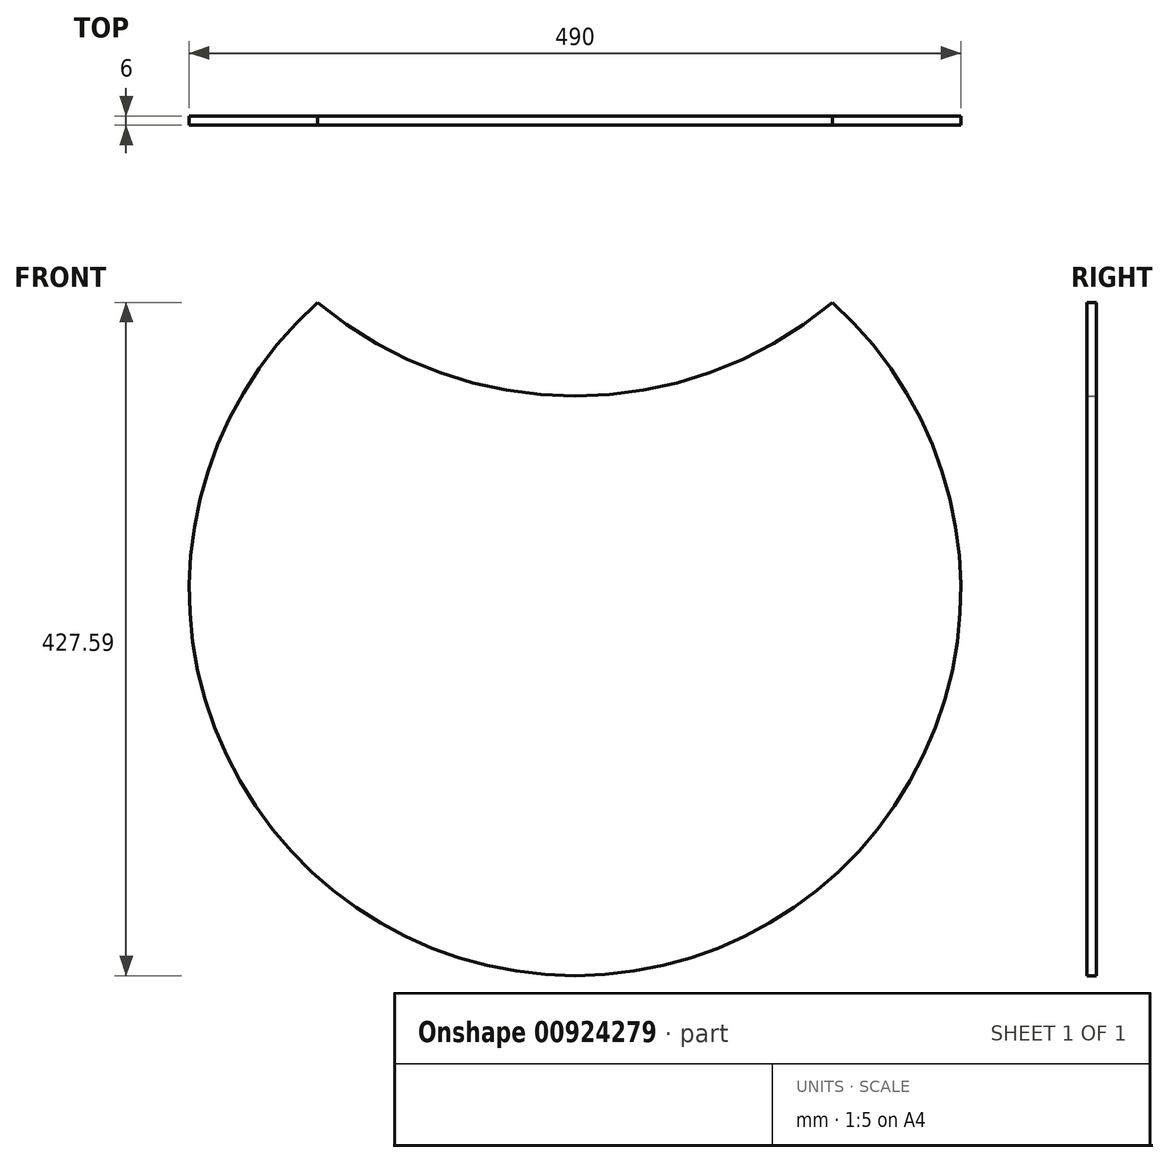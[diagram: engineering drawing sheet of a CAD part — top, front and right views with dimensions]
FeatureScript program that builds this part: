
annotation { "Feature Type Name" : "Feature", "Feature Type Description" : "" }
export const myFeature = defineFeature(function(context is Context, id is Id, definition is map)
    precondition{}
    {
        {
            var Q0;
            Q0=qCreatedBy(makeId("Front.planeOp"),FACE);
            var sketch = newSketch(context, id + "F0", { "sketchPlane" : qUnion([Q0])});
            skCircle(sketch, "E0", {"center": v(0, 0) * mm, "radius": 245 * mm});
            skArc(sketch, "E1", {"start": v(-163.36, 182.59) * mm, "mid": v(0, 123.08) * mm, "end": v(163.36, 182.59) * mm});
            skSolve(sketch);
        }
        {
            var Q0;
            {var subQ0=sQuery(id+"F0.wireOp",EDGE,"E1");Q0=makeQuery(id+"F0.imprint","IMPRINT",FACE,{"disambiguationData":[TD([[makeQuery(id+"F0.imprint","IMPRINT",EDGE,{"derivedFrom":subQ0}),-1.0]])]});}
            extrude(context, id + "F1", {"entities" : qUnion([Q0]), "depth" : 6 * mm, "offsetDistance" : 25.4 * mm});
        }
    });
